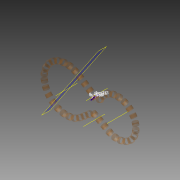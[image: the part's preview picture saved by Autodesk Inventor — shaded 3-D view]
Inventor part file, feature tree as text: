
AUTODESK INVENTOR PART (.ipt)
format: ipt  version: 2014 SP1 (Build 180222100, 222)  size: 275,456 bytes
history: native  units: mm (DEFAULTED — no unit token found)
features: other x48, extrude x42, sketch x2, plane x1, pattern_linear x1
ambient origin geometry x8: Origin, YZ Plane, XZ Plane, XY Plane, X Axis, Y Axis, Z Axis, Center Point
bodies: Body1 (feature_tree), Body2 (feature_tree), Body3 (feature_tree), Body4 (feature_tree), Body5 (feature_tree), Body6 (feature_tree), Body7 (feature_tree), Body8 (feature_tree), Body9 (feature_tree), Body10 (feature_tree), Body11 (feature_tree), Body12 (feature_tree), Body13 (feature_tree), Body14 (feature_tree), Body15 (feature_tree), Body16 (feature_tree), Body17 (feature_tree), Body18 (feature_tree), Body19 (feature_tree), Body20 (feature_tree), Body21 (feature_tree), Body22 (feature_tree), Body23 (feature_tree), Body24 (feature_tree), Body25 (feature_tree), Body26 (feature_tree), Body27 (feature_tree), Body28 (feature_tree), Body29 (feature_tree), Body30 (feature_tree), Body31 (feature_tree), Body32 (feature_tree), Body33 (feature_tree), Body34 (feature_tree), Body35 (feature_tree), Body36 (feature_tree), Body37 (feature_tree), Body38 (feature_tree), Body39 (feature_tree), Body40 (feature_tree), Body41 (feature_tree), Body42 (feature_tree)
feature tree (94):
  sketch  "Sketch Path"  dims[d1=10.6172mm d2=7.9375mm d3=2.682204mm d5=6.981317mm d7=0.0mm d8=0.0mm d9=0.0mm d10=0.0mm d11=0.0mm d12=5.08mm d13=0.0mm d14=420.0mm]
  other  "Cross Section Plane"
  other  "Work Axis1"
  other  "Work Axis2"
  other  "Work Axis3"
  other  "Work Axis4"
  other  "Cross Section"
  plane  "Work Plane2"
  pattern_linear  "Rectangular Pattern1"  Spacing1=7.9375mm  [1 undecoded]
  sketch  "Sketch3"  dims[d0=0.0mm]
  other  "Srf1"
  other  "Srf2"
  other  "Srf3"
  other  "Srf4"
  other  "Srf5"
  other  "Srf6"
  other  "Srf7"
  other  "Srf8"
  other  "Srf9"
  other  "Srf10"
  other  "Srf11"
  other  "Srf12"
  other  "Srf13"
  other  "Srf14"
  other  "Srf15"
  other  "Srf16"
  other  "Srf17"
  other  "Srf18"
  other  "Srf19"
  other  "Srf20"
  other  "Srf21"
  other  "Srf22"
  other  "Srf23"
  other  "Srf24"
  other  "Srf25"
  other  "Srf26"
  other  "Srf27"
  other  "Srf28"
  other  "Srf29"
  other  "Srf30"
  other  "Srf31"
  other  "Srf32"
  other  "Srf33"
  other  "Srf34"
  other  "Srf35"
  other  "Srf36"
  other  "Srf37"
  other  "Srf38"
  other  "Srf39"
  other  "Srf40"
  other  "Srf41"
  other  "Srf42"
  extrude  "ExtrusionSrf1"  Depth=6.981317mm
  extrude  "ExtrusionSrf2"  Depth=6.981317mm
  extrude  "ExtrusionSrf3"  TaperAngle=0.0deg  [1 undecoded]
  extrude  "ExtrusionSrf4"  TaperAngle=0.0deg  [1 undecoded]
  extrude  "ExtrusionSrf5"  Depth=6.981317mm TaperAngle=0.0deg
  extrude  "ExtrusionSrf6"  Depth=6.981317mm
  extrude  "ExtrusionSrf7"  [1 undecoded]
  extrude  "ExtrusionSrf8"  [1 undecoded]
  extrude  "ExtrusionSrf9"  [1 undecoded]
  extrude  "ExtrusionSrf10"  [1 undecoded]
  extrude  "ExtrusionSrf11"  [1 undecoded]
  extrude  "ExtrusionSrf12"  [1 undecoded]
  extrude  "ExtrusionSrf13"  [1 undecoded]
  extrude  "ExtrusionSrf14"  [1 undecoded]
  extrude  "ExtrusionSrf15"  [1 undecoded]
  extrude  "ExtrusionSrf16"  [1 undecoded]
  extrude  "ExtrusionSrf17"  [1 undecoded]
  extrude  "ExtrusionSrf18"  [1 undecoded]
  extrude  "ExtrusionSrf19"  [1 undecoded]
  extrude  "ExtrusionSrf20"  [1 undecoded]
  extrude  "ExtrusionSrf21"  [1 undecoded]
  extrude  "ExtrusionSrf22"  [1 undecoded]
  extrude  "ExtrusionSrf23"  [1 undecoded]
  extrude  "ExtrusionSrf24"  [1 undecoded]
  extrude  "ExtrusionSrf25"  [1 undecoded]
  extrude  "ExtrusionSrf26"  [1 undecoded]
  extrude  "ExtrusionSrf27"  [1 undecoded]
  extrude  "ExtrusionSrf28"  [1 undecoded]
  extrude  "ExtrusionSrf29"  [1 undecoded]
  extrude  "ExtrusionSrf30"  [1 undecoded]
  extrude  "ExtrusionSrf31"  [1 undecoded]
  extrude  "ExtrusionSrf32"  [1 undecoded]
  extrude  "ExtrusionSrf33"  [1 undecoded]
  extrude  "ExtrusionSrf34"  [1 undecoded]
  extrude  "ExtrusionSrf35"  [1 undecoded]
  extrude  "ExtrusionSrf36"  [1 undecoded]
  extrude  "ExtrusionSrf37"  [1 undecoded]
  extrude  "ExtrusionSrf38"  [1 undecoded]
  extrude  "ExtrusionSrf39"  [1 undecoded]
  extrude  "ExtrusionSrf40"  [1 undecoded]
  extrude  "ExtrusionSrf41"  [1 undecoded]
  extrude  "ExtrusionSrf42"  [1 undecoded]
note: 39 required parameter values undecoded (feature->parameter linkage not recoverable at this tier; creation-order binding heuristic only, values carry confidence <= 0.55)
